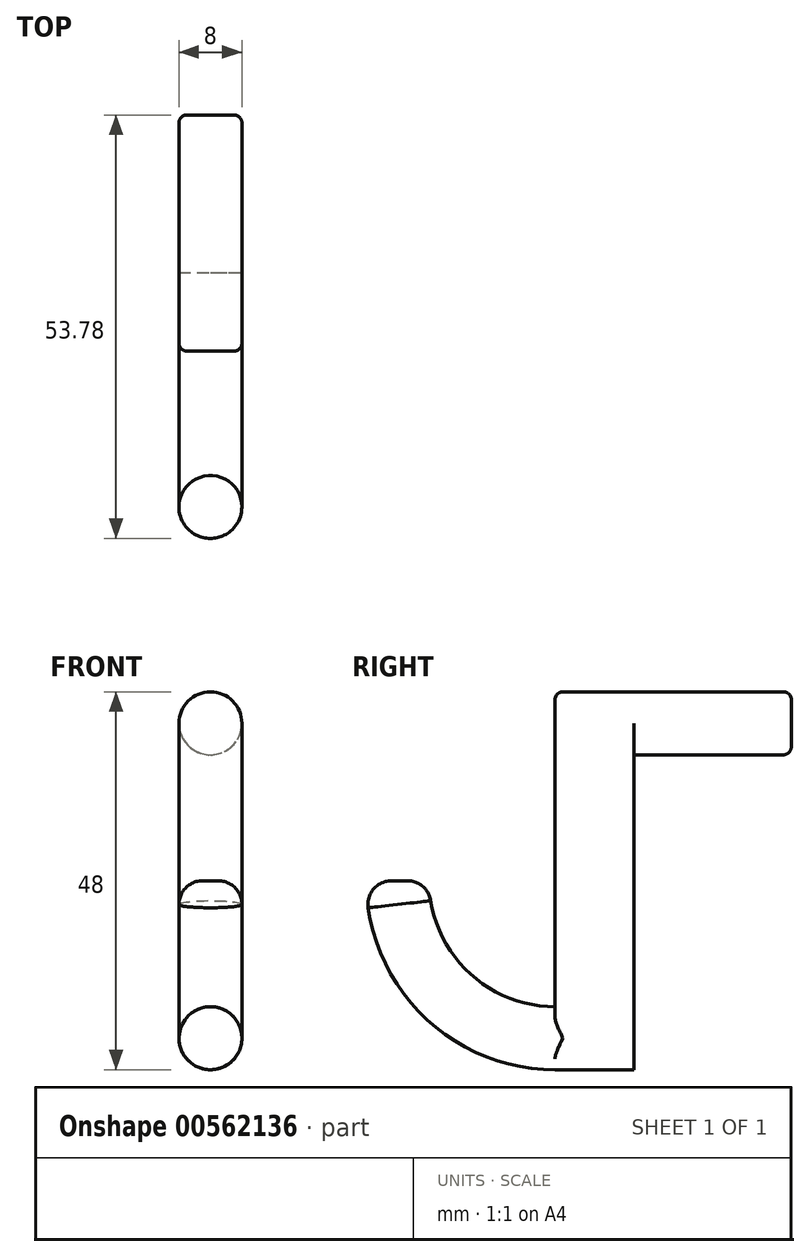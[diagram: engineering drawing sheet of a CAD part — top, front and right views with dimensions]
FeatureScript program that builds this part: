
annotation { "Feature Type Name" : "Feature", "Feature Type Description" : "" }
export const myFeature = defineFeature(function(context is Context, id is Id, definition is map)
    precondition{}
    {
        {
            var Q0;
            Q0=qCreatedBy(makeId("Front.planeOp"),FACE);
            var sketch = newSketch(context, id + "F0", { "sketchPlane" : qUnion([Q0])});
            skCircle(sketch, "E0", {"center": v(0, 20) * mm, "radius": 4 * mm});
            skSolve(sketch);
        }
        {
            var Q0;
            Q0=makeQuery(id+"F0.imprint","IMPRINT",FACE,{"disambiguationData":[TD([[makeQuery(id+"F0.imprint","IMPRINT",EDGE,{"derivedFrom":sQuery(id+"F0.wireOp",EDGE,"E0")}),1.0]])]});
            extrude(context, id + "F1", {"entities" : qUnion([Q0]), "oppositeDirection" : true, "depth" : 20 * mm, "offsetDistance" : 25 * mm});
        }
        {
            var Q0;
            Q0=qCreatedBy(makeId("Front.planeOp"),FACE);
            var sketch = newSketch(context, id + "F2", { "sketchPlane" : qUnion([Q0])});
            skLineSegment(sketch, "E1", {"start": v(0, 20) * mm, "end": v(0, -20) * mm, "construction": true});
            skLineSegment(sketch, "E2.0", {"start": v(-4, 20) * mm, "end": v(-4, -20) * mm});
            skLineSegment(sketch, "E3.0", {"start": v(4, 20) * mm, "end": v(4, -20) * mm});
            skArc(sketch, "E4", {"start": v(4, 20) * mm, "mid": v(0, 24) * mm, "end": v(-4, 20) * mm});
            skArc(sketch, "E5.MirrorC", {"start": v(4, -20) * mm, "mid": v(0, -24) * mm, "end": v(-4, -20) * mm});
            skSolve(sketch);
        }
        {
            var Q0;
            Q0=makeQuery(id+"F2.imprint","IMPRINT",FACE,{"disambiguationData":[TD([[makeQuery(id+"F2.imprint","IMPRINT",EDGE,{"derivedFrom":sQuery(id+"F2.wireOp",EDGE,"E2.0")}),1.0]])]});
            extrude(context, id + "F3", {"entities" : qUnion([Q0]), "operationType" : NewBodyOperationType.ADD, "depth" : 10 * mm, "offsetDistance" : 25 * mm});
        }
        {
            var Q0;
            Q0=makeQuery(id+"F3.opExtrude","CAP_FACE",FACE,{"disambiguationData":[OSD([sQuery(id+"F2.wireOp",EDGE,"E2.0"),sQuery(id+"F2.wireOp",EDGE,"E3.0"),sQuery(id+"F2.wireOp",EDGE,"E4"),sQuery(id+"F2.wireOp",EDGE,"E5.MirrorC")])],"isStart":false});
            var sketch = newSketch(context, id + "F4", { "sketchPlane" : qUnion([Q0])});
            skCircle(sketch, "E6", {"center": v(0, -20) * mm, "radius": 4 * mm});
            skLineSegment(sketch, "E7", {"start": v(0, 0) * mm, "end": v(0, -20) * mm, "construction": true});
            skLineSegment(sketch, "E8", {"start": v(-4, 0) * mm, "end": v(4, 0) * mm, "construction": true});
            skSolve(sketch);
        }
        {
            var Q0;
            Q0 = qSketchRegion(id + "F4", true);
            var Q1;
            Q1=sQuery(id+"F4.wireOp",EDGE,"E8");
            revolve(context, id + "F5", {"operationType" : NewBodyOperationType.ADD, "entities" : qUnion([Q0]), "axis" : qUnion([Q1]), "revolveType" : RevolveType.ONE_DIRECTION, "oppositeDirection" : true, "angle" : 90 * degree});
        }
        {
            var Q0;
            Q0=makeQuery(id+"F5.opRevolve","CAP_FACE",FACE,{"disambiguationData":[OSD([sQuery(id+"F4.wireOp",EDGE,"E6")])],"isStart":false});
            fillet(context, id + "F6", {"entities" : qUnion([Q0]), "radius" : 3 * mm, "tangentPropagation" : true, "allowEdgeOverflow" : false});
        }
        {
            var Q0;
            Q0=makeQuery(id+"F3.opExtrude","CAP_EDGE",EDGE,{"disambiguationData":[OSD([sQuery(id+"F2.wireOp",EDGE,"E3.0")])],"isStart":false});
            var Q1;
            Q1=makeQuery(id+"F1.opExtrude","CAP_FACE",FACE,{"disambiguationData":[OSD([sQuery(id+"F0.wireOp",EDGE,"E0")])],"isStart":false});
            fillet(context, id + "F7", {"entities" : qUnion([Q0, Q1]), "radius" : 1 * mm, "tangentPropagation" : true, "allowEdgeOverflow" : false});
        }
    });
